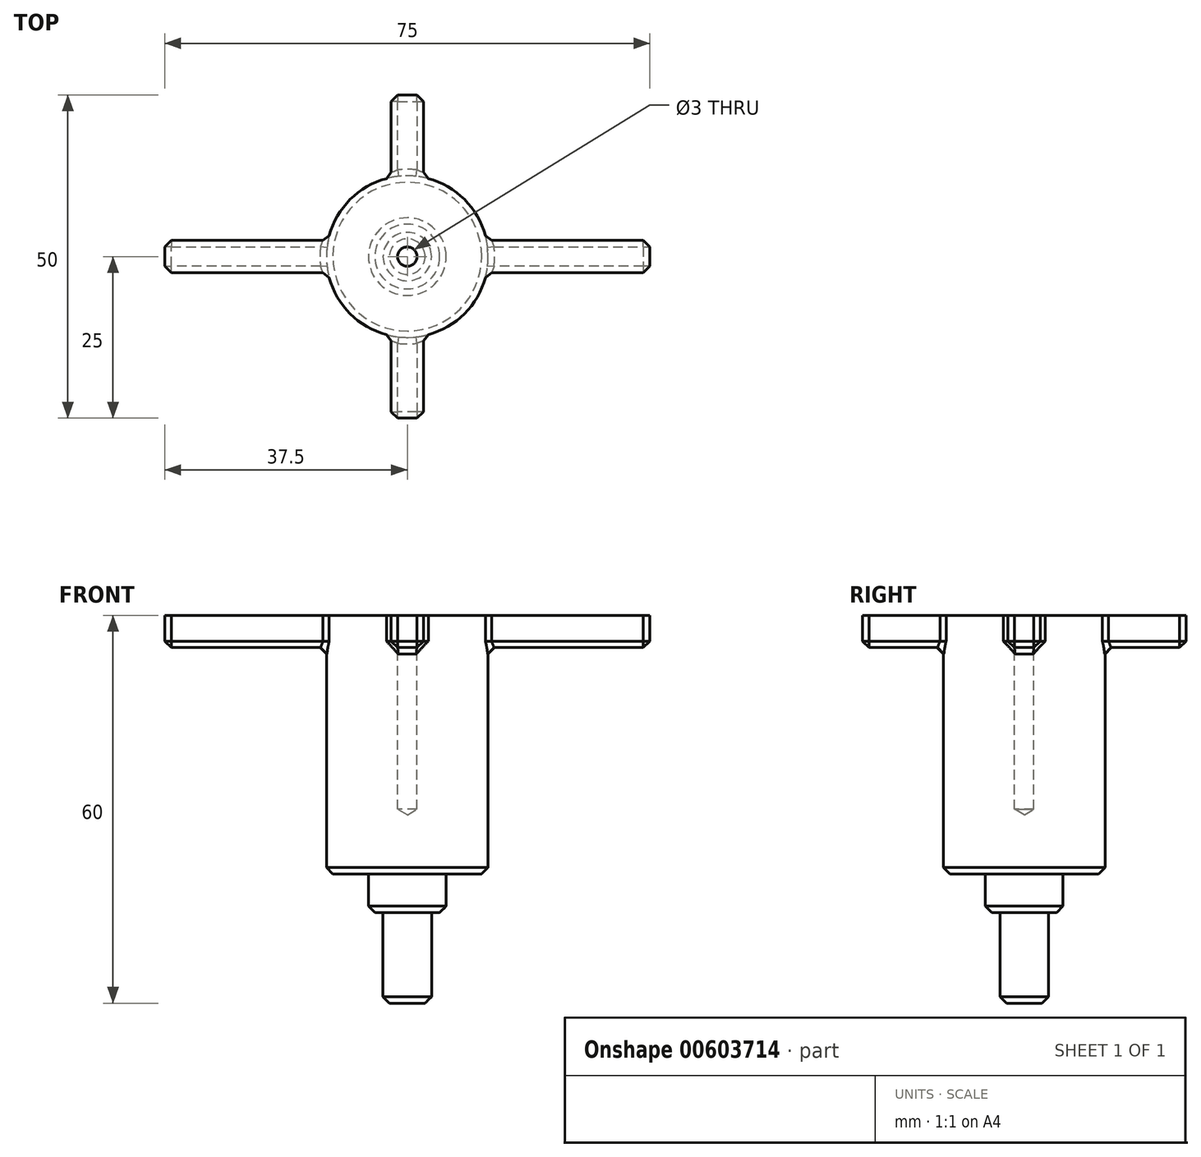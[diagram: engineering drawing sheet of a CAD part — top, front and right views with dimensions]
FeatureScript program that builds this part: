
annotation { "Feature Type Name" : "Feature", "Feature Type Description" : "" }
export const myFeature = defineFeature(function(context is Context, id is Id, definition is map)
    precondition{}
    {
        {
            var Q0;
            Q0=qCreatedBy(makeId("Top.planeOp"),FACE);
            var sketch = newSketch(context, id + "F0", { "sketchPlane" : qUnion([Q0])});
            skCircle(sketch, "E0", {"center": v(0, 0) * mm, "radius": 12.5 * mm});
            skCircle(sketch, "E1", {"center": v(0, 0) * mm, "radius": 3.75 * mm});
            skCircle(sketch, "E2", {"center": v(0, 0) * mm, "radius": 6 * mm});
            skSolve(sketch);
        }
        {
            var Q0;
            Q0=makeQuery(id+"F0.imprint","IMPRINT",FACE,{"disambiguationData":[TD([[makeQuery(id+"F0.imprint","IMPRINT",EDGE,{"derivedFrom":sQuery(id+"F0.wireOp",EDGE,"E1")}),1.0]])]});
            extrude(context, id + "F1", {"entities" : qUnion([Q0]), "depth" : 30 * mm, "offsetDistance" : 25 * mm});
        }
        {
            var Q0;
            Q0=makeQuery(id+"F0.imprint","IMPRINT",FACE,{"disambiguationData":[TD([[makeQuery(id+"F0.imprint","IMPRINT",EDGE,{"derivedFrom":sQuery(id+"F0.wireOp",EDGE,"E0")}),1.0]])]});
            var Q1;
            Q1=makeQuery(id+"F0.imprint","IMPRINT",FACE,{"disambiguationData":[TD([[makeQuery(id+"F0.imprint","IMPRINT",EDGE,{"derivedFrom":sQuery(id+"F0.wireOp",EDGE,"E1")}),-1.0]])]});
            var Q2;
            Q2=makeQuery(id+"F0.imprint","IMPRINT",FACE,{"disambiguationData":[TD([[makeQuery(id+"F0.imprint","IMPRINT",EDGE,{"derivedFrom":sQuery(id+"F0.wireOp",EDGE,"E1")}),1.0]])]});
            extrude(context, id + "F2", {"entities" : qUnion([Q0, Q1, Q2]), "operationType" : NewBodyOperationType.ADD, "depth" : 60 * mm, "offsetDistance" : 25 * mm, "hasSecondDirection" : true, "secondDirectionOppositeDirection" : false, "secondDirectionDepth" : 20 * mm});
        }
        {
            var Q0;
            Q0=makeQuery(id+"F0.imprint","IMPRINT",FACE,{"disambiguationData":[TD([[makeQuery(id+"F0.imprint","IMPRINT",EDGE,{"derivedFrom":sQuery(id+"F0.wireOp",EDGE,"E1")}),-1.0]])]});
            extrude(context, id + "F3", {"entities" : qUnion([Q0]), "operationType" : NewBodyOperationType.ADD, "depth" : 20 * mm, "offsetDistance" : 25 * mm, "hasSecondDirection" : true, "secondDirectionOppositeDirection" : false, "secondDirectionDepth" : 14 * mm});
        }
        {
            var Q0;
            {var subQ0=sQuery(id+"F0.wireOp",EDGE,"E1");Q0=makeQuery(id+"F2.boolean.opBoolean","MERGE",FACE,{"derivedFrom":[makeQuery(id+"F1.opExtrude","CAP_FACE",FACE,{"disambiguationData":[OSD([subQ0])],"isStart":false}),makeQuery(id+"F2.opExtrude","CAP_FACE",FACE,{"disambiguationData":[OSD([sQuery(id+"F0.wireOp",EDGE,"E0"),subQ0])],"isStart":false})]});}
            cPlane(context, id + "F4", {"entities" : qUnion([Q0]), "cplaneType" : CPlaneType.OFFSET, "offset" : 0 * mm, "width" : 150 * mm, "height" : 150 * mm});
        }
        {
            var Q0;
            Q0=qCreatedBy(id+"F4.planeOp",FACE);
            var sketch = newSketch(context, id + "F5", { "sketchPlane" : qUnion([Q0])});
            skPoint(sketch, "E3", {"position": v(0, 0) * mm});
            skLineSegment(sketch, "E4.bottom", {"start": v(37.5, 2.5) * mm, "end": v(-37.5, 2.5) * mm});
            skLineSegment(sketch, "E4.top", {"start": v(37.5, -2.5) * mm, "end": v(-37.5, -2.5) * mm});
            skLineSegment(sketch, "E4.left", {"start": v(37.5, 2.5) * mm, "end": v(37.5, -2.5) * mm});
            skLineSegment(sketch, "E4.right", {"start": v(-37.5, 2.5) * mm, "end": v(-37.5, -2.5) * mm});
            skLineSegment(sketch, "E5.bottom", {"start": v(2.5, 25) * mm, "end": v(-2.5, 25) * mm});
            skLineSegment(sketch, "E5.top", {"start": v(2.5, -25) * mm, "end": v(-2.5, -25) * mm});
            skLineSegment(sketch, "E5.left", {"start": v(2.5, 25) * mm, "end": v(2.5, -25) * mm});
            skLineSegment(sketch, "E5.right", {"start": v(-2.5, 25) * mm, "end": v(-2.5, -25) * mm});
            skSolve(sketch);
        }
        {
            var Q0;
            Q0=sQuery(id+"F5.wireOp",VERTEX,"E3");
            var Q1;
            Q1=makeQuery(id+"F1.opExtrude","SWEPT_BODY",BODY,{"disambiguationData":[OSD([sQuery(id+"F0.wireOp",EDGE,"E1")])]});
            hole(context, id + "F6", {"style" : HoleStyle.SIMPLE, "endStyle" : HoleEndStyle.BLIND, "holeDiameter" : 3 * mm, "majorDiameter" : 5 * mm, "holeDepth" : 30 * mm, "isTappedThrough" : true, "tappedDepth" : 12 * mm, "tapClearance" : 3, "startFromSketch" : true, "locations" : qUnion([Q0]), "scope" : qUnion([Q1])});
        }
        {
            var Q0;
            {var subQ5=sQuery(id+"F5.wireOp",EDGE,"E5.bottom");Q0=makeQuery(id+"F5.imprint","IMPRINT",FACE,{"disambiguationData":[TD([[makeQuery(id+"F5.imprint","IMPRINT",EDGE,{"derivedFrom":subQ5}),1.0]])]});}
            var Q1;
            {var subQ0=sQuery(id+"F5.wireOp",EDGE,"E4.right");Q1=makeQuery(id+"F5.imprint","IMPRINT",FACE,{"disambiguationData":[TD([[makeQuery(id+"F5.imprint","IMPRINT",EDGE,{"derivedFrom":subQ0}),1.0]])]});}
            var Q2;
            {var subQ5=sQuery(id+"F5.wireOp",EDGE,"E5.top");Q2=makeQuery(id+"F5.imprint","IMPRINT",FACE,{"disambiguationData":[TD([[makeQuery(id+"F5.imprint","IMPRINT",EDGE,{"derivedFrom":subQ5}),-1.0]])]});}
            var Q3;
            {var subQ0=sQuery(id+"F5.wireOp",EDGE,"E4.left");Q3=makeQuery(id+"F5.imprint","IMPRINT",FACE,{"disambiguationData":[TD([[makeQuery(id+"F5.imprint","IMPRINT",EDGE,{"derivedFrom":subQ0}),-1.0]])]});}
            extrude(context, id + "F7", {"entities" : qUnion([Q0, Q1, Q2, Q3]), "operationType" : NewBodyOperationType.ADD, "oppositeDirection" : true, "depth" : 5 * mm, "offsetDistance" : 25 * mm});
        }
        {
            var Q0;
            Q0=makeQuery(id+"F3.opExtrude","CAP_EDGE",EDGE,{"disambiguationData":[OSD([sQuery(id+"F0.wireOp",EDGE,"E2")])],"isStart":true});
            var Q1;
            Q1=makeQuery(id+"F2.opExtrude","CAP_EDGE",EDGE,{"disambiguationData":[OSD([sQuery(id+"F0.wireOp",EDGE,"E0")])],"isStart":true});
            var Q2;
            Q2=makeQuery(id+"F1.opExtrude","CAP_EDGE",EDGE,{"disambiguationData":[OSD([sQuery(id+"F0.wireOp",EDGE,"E1")])],"isStart":true});
            var Q3;
            Q3=makeQuery(id+"F7.opExtrude","CAP_FACE",FACE,{"disambiguationData":[OSD([sQuery(id+"F5.wireOp",EDGE,"E4.bottom"),sQuery(id+"F5.wireOp",EDGE,"E4.top"),sQuery(id+"F5.wireOp",EDGE,"E4.right"),sQuery(id+"F5.wireOp",EDGE,"E5.right")])],"isStart":false});
            var Q4;
            Q4=makeQuery(id+"F7.opExtrude","CAP_FACE",FACE,{"disambiguationData":[OSD([sQuery(id+"F5.wireOp",EDGE,"E4.bottom"),sQuery(id+"F5.wireOp",EDGE,"E5.bottom"),sQuery(id+"F5.wireOp",EDGE,"E5.left"),sQuery(id+"F5.wireOp",EDGE,"E5.right")])],"isStart":false});
            var Q5;
            Q5=makeQuery(id+"F7.opExtrude","CAP_FACE",FACE,{"disambiguationData":[OSD([sQuery(id+"F5.wireOp",EDGE,"E4.bottom"),sQuery(id+"F5.wireOp",EDGE,"E4.top"),sQuery(id+"F5.wireOp",EDGE,"E4.left"),sQuery(id+"F5.wireOp",EDGE,"E5.left")])],"isStart":false});
            var Q6;
            Q6=makeQuery(id+"F7.opExtrude","CAP_FACE",FACE,{"disambiguationData":[OSD([sQuery(id+"F5.wireOp",EDGE,"E4.top"),sQuery(id+"F5.wireOp",EDGE,"E5.top"),sQuery(id+"F5.wireOp",EDGE,"E5.left"),sQuery(id+"F5.wireOp",EDGE,"E5.right")])],"isStart":false});
            var Q7;
            Q7=makeQuery(id+"F7.opExtrude","SWEPT_EDGE",EDGE,{"disambiguationData":[OSD([sQuery(id+"F5.wireOp",EDGE,"E5.top"),sQuery(id+"F5.wireOp",EDGE,"E5.right")])]});
            var Q8;
            Q8=makeQuery(id+"F7.opExtrude","SWEPT_EDGE",EDGE,{"disambiguationData":[OSD([sQuery(id+"F5.wireOp",EDGE,"E5.top"),sQuery(id+"F5.wireOp",EDGE,"E5.left")])]});
            var Q9;
            Q9=makeQuery(id+"F7.opExtrude","SWEPT_EDGE",EDGE,{"disambiguationData":[OSD([sQuery(id+"F5.wireOp",EDGE,"E4.top"),sQuery(id+"F5.wireOp",EDGE,"E4.left")])]});
            var Q10;
            Q10=makeQuery(id+"F7.opExtrude","SWEPT_EDGE",EDGE,{"disambiguationData":[OSD([sQuery(id+"F5.wireOp",EDGE,"E4.bottom"),sQuery(id+"F5.wireOp",EDGE,"E4.left")])]});
            var Q11;
            Q11=makeQuery(id+"F7.opExtrude","SWEPT_EDGE",EDGE,{"disambiguationData":[OSD([sQuery(id+"F5.wireOp",EDGE,"E5.bottom"),sQuery(id+"F5.wireOp",EDGE,"E5.right")])]});
            var Q12;
            Q12=makeQuery(id+"F7.opExtrude","SWEPT_EDGE",EDGE,{"disambiguationData":[OSD([sQuery(id+"F5.wireOp",EDGE,"E5.bottom"),sQuery(id+"F5.wireOp",EDGE,"E5.left")])]});
            var Q13;
            Q13=makeQuery(id+"F7.opExtrude","SWEPT_EDGE",EDGE,{"disambiguationData":[OSD([sQuery(id+"F5.wireOp",EDGE,"E4.top"),sQuery(id+"F5.wireOp",EDGE,"E4.right")])]});
            var Q14;
            Q14=makeQuery(id+"F7.opExtrude","SWEPT_EDGE",EDGE,{"disambiguationData":[OSD([sQuery(id+"F5.wireOp",EDGE,"E4.bottom"),sQuery(id+"F5.wireOp",EDGE,"E4.right")])]});
            chamfer(context, id + "F8", {"entities" : qUnion([Q0, Q1, Q2, Q3, Q4, Q5, Q6, Q7, Q8, Q9, Q10, Q11, Q12, Q13, Q14]), "width" : 1 * mm, "tangentPropagation" : true});
        }
    });
